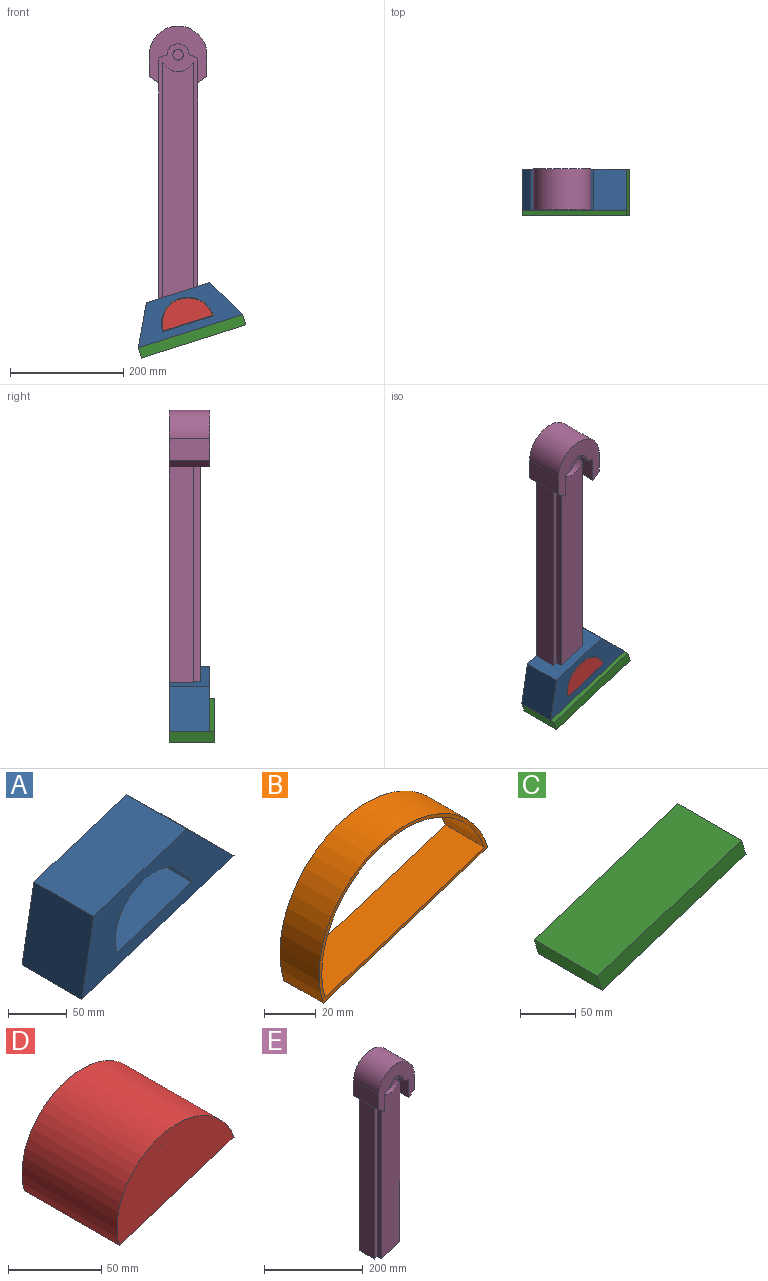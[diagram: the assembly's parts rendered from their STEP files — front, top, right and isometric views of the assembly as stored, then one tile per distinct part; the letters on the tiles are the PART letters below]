
ASSEMBLY  parts=5 mates=4
PART A: 8 faces, bbox 183.7x72.1x115 mm
  f0: plane 72.14x57.54mm, normal (0.7,0,0.71), area 5828mm2, adj f1,f5,f6,f7
  f1: plane 183.65x72.14mm, normal (0.3,0,-0.95), area 13899.8mm2, adj f0,f2,f6,f7
  f2: plane 79.52x72.14mm, normal (-0.98,0,0.18), area 5828mm2, adj f1,f5,f6,f7
  f3: plane 90x72.14mm, normal (-0.3,0,0.95), area 6811.8mm2, adj f4,f6,f7
  f4: cylinder r=47.22mm len=92.22mm, axis (0,1,0), area 10700mm2, adj f3,f6,f7
  f5: plane 111.83x72.14mm, normal (-0.3,0,0.95), area 8463.7mm2, adj f0,f2,f6,f7
  f6: plane 183.65x115.03mm, normal (0,-1,0), area 7576.2mm2, adj f0,f1,f2,f3,f4,f5
  f7: plane 183.65x115.03mm, normal (0,1,0), area 7576.2mm2, adj f0,f1,f2,f3,f4,f5
PART B: 6 faces, bbox 92.2x21.3x61.5 mm
  f0: plane 87.05x27.64mm, normal (-0.3,0,0.95), area 1948.7mm2, adj f3,f4,f5
  f1: cylinder r=47.22mm len=92.22mm, axis (0,1,0), area 3164.8mm2, adj f2,f4,f5
  f2: plane 90x28.58mm, normal (0.3,0,-0.95), area 2014.8mm2, adj f1,f4,f5
  f3: cylinder r=45.69mm len=88.75mm, axis (0,1,0), area 2997.6mm2, adj f0,f4,f5
  f4: plane 92.22x61.51mm, normal (0,-1,0), area 361.6mm2, adj f0,f1,f2,f3
  f5: plane 92.22x61.51mm, normal (0,1,0), area 361.6mm2, adj f0,f1,f2,f3
PART C: 6 faces, bbox 189.4x81x76.4 mm
  f0: plane 183.65x81.03mm, normal (-0.3,0,0.95), area 15612.8mm2, adj f1,f3,f4,f5
  f1: plane 81.03x18.08mm, normal (0.95,0,0.3), area 1537mm2, adj f0,f2,f4,f5
  f2: plane 183.65x81.03mm, normal (0.3,0,-0.95), area 15612.8mm2, adj f1,f3,f4,f5
  f3: plane 81.03x18.08mm, normal (-0.95,0,-0.3), area 1537mm2, adj f0,f2,f4,f5
  f4: plane 189.39x76.4mm, normal (0,-1,0), area 3655.2mm2, adj f0,f1,f2,f3
  f5: plane 189.39x76.4mm, normal (0,1,0), area 3655.2mm2, adj f0,f1,f2,f3
PART D: 7 faces, bbox 88.8x72.1x58.1 mm
  f0: plane 87.05x72.14mm, normal (0.3,0,-0.95), area 6588.3mm2, adj f4,f5,f6
  f1: plane 72.14x0.44mm, normal (-0.95,0,-0.3), area 33.1mm2, adj f2,f3,f5,f6
  f2: plane 72.14x0.44mm, normal (1,0,0), area 31.5mm2, adj f1,f3,f5,f6
  f3: plane 72.14x0.14mm, normal (0,0,1), area 10mm2, adj f1,f2,f5,f6
  f4: cylinder r=45.69mm len=88.75mm, axis (0,1,0), area 10134.7mm2, adj f0,f5,f6
  f5: plane 88.75x58.06mm, normal (0,-1,0), area 3140.1mm2, adj f0,f1,f2,f3,f4
  f6: plane 88.75x58.06mm, normal (0,1,0), area 3140.1mm2, adj f0,f1,f2,f3,f4
PART E: 22 faces, bbox 101.6x72.1x481.5 mm
  f0: plane 44.06x29.21mm, normal (-1,0,0), area 1286.9mm2, adj f1,f2,f10,f16
  f1: plane 72.14x16.28mm, normal (0.58,0,-0.81), area 1442.9mm2, adj f0,f9,f10,f11,f13
  f2: plane 29.21x15.26mm, normal (-0.35,0,-0.94), area 475.6mm2, adj f0,f3,f10,f16
  f3: cylinder r=19.26mm len=38.52mm, axis (0,1,0), area 1767.3mm2, adj f2,f4,f10,f16
  f4: plane 29.21x15.26mm, normal (0.35,0,-0.94), area 475.6mm2, adj f3,f5,f10,f16
  f5: plane 44.06x29.21mm, normal (1,0,0), area 1286.9mm2, adj f4,f6,f10,f16
  f6: plane 72.14x16.28mm, normal (-0.58,0,-0.81), area 1442.9mm2, adj f5,f7,f10,f11,f12
  f7: plane 72.14x38.1mm, normal (-1,0,0), area 2748.4mm2, adj f6,f8,f10,f11
  f8: cylinder r=50.8mm len=101.6mm, axis (0,1,0), area 11512.4mm2, adj f7,f9,f10,f11
  f9: plane 72.14x38.1mm, normal (1,0,0), area 2748.4mm2, adj f1,f8,f10,f11
  f10: plane 101.6x100.53mm, normal (0,-1,0), area 4987.2mm2, adj f0,f1,f2,f3,f4,f5,f6,f7
  f11: plane 481.53x101.6mm, normal (0,1,0), area 34465.8mm2, adj f1,f6,f7,f8,f9,f12,f13,f14
  f12: plane 381x42.93mm, normal (-1,0,0), area 16354.8mm2, adj f6,f11,f14,f16
  f13: plane 359.07x42.93mm, normal (1,0,0), area 15413.6mm2, adj f1,f11,f14,f16
  f14: plane 69.05x54.86mm, normal (0.3,0,-0.95), area 3783.3mm2, adj f11,f12,f13,f16,f17,f18,f20
  f15: cylinder r=9.27mm len=21.59mm, axis (0,1,0), area 1258.2mm2, adj f16,f21
  f16: plane 449.98x69.05mm, normal (0,-1,0), area 7979.6mm2, adj f0,f2,f3,f4,f5,f12,f13,f14
  f17: plane 398.32x11.94mm, normal (1,0,0), area 4755.1mm2, adj f14,f16,f19,f20
  f18: plane 415.4x11.94mm, normal (-1,0,0), area 4959mm2, adj f14,f16,f19,f20
  f19: cylinder r=29.83mm len=53.78mm, axis (0,1,0), area 800mm2, adj f16,f17,f18,f20
  f20: plane 415.4x53.78mm, normal (0,-1,0), area 21228.8mm2, adj f14,f17,f18,f19
  f21: plane 18.55x18.55mm, normal (0,-1,0), area 270.2mm2, adj f15
PLACE A t=(437.83,169.34,370.13)mm
PLACE B t=(437.83,169.34,370.13)mm
PLACE C t=(437.83,169.34,370.13)mm
PLACE D t=(437.83,169.34,370.13)mm
PLACE E t=(459.22,169.34,376.92)mm
MATE fastened A.f5 <-> E.f14  axis (-0.3,0,0.95) through (139.18,169.34,-4.74)mm
MATE fastened A.f1 <-> C.f0  axis (0.3,0,-0.95) through (160.81,169.34,-72.86)mm
MATE fastened A.f3 <-> B.f2  axis (-0.3,0,0.95) through (156.68,169.34,-59.86)mm
MATE fastened B.f0 <-> D.f0  axis (-0.3,0,0.95) through (156.22,169.34,-58.41)mm
